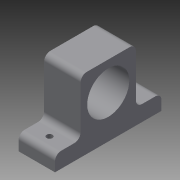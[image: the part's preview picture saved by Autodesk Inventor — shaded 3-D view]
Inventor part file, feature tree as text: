
AUTODESK INVENTOR PART (.ipt)
format: ipt  version: 2015 (Build 190159000, 159)  size: 130,048 bytes
history: native  units: in
note: dims shown in document units (in); Inventor stores cm internally (conversion verified against a paired STEP export)
features: extrude x2, fillet x2, sketch x2, projected_geometry x2
ambient origin geometry x8: Origin, YZ Plane, XZ Plane, XY Plane, X Axis, Y Axis, Z Axis, Center Point
bodies: Solid1 (feature_tree)
feature tree (8):
  extrude  "Extrusion1"  Depth=0.75in TaperAngle=0.0deg
  fillet  "Fillet1"  Radius=0.125in
  extrude  "Extrusion2"  Depth=0.75in TaperAngle=0.0deg
  fillet  "Fillet2"  Radius=0.0625in
  sketch  "Sketch1"  dims[d0=0.865in d1=0.75in d2=0.0in d3=0.125in]
  sketch  "Sketch2"  dims[d4=0.1209in d5=0.75in d6=0.0in d7=0.0625in]
  projected_geometry  "Projected Loop1"
  projected_geometry  "Projected Loop2"
